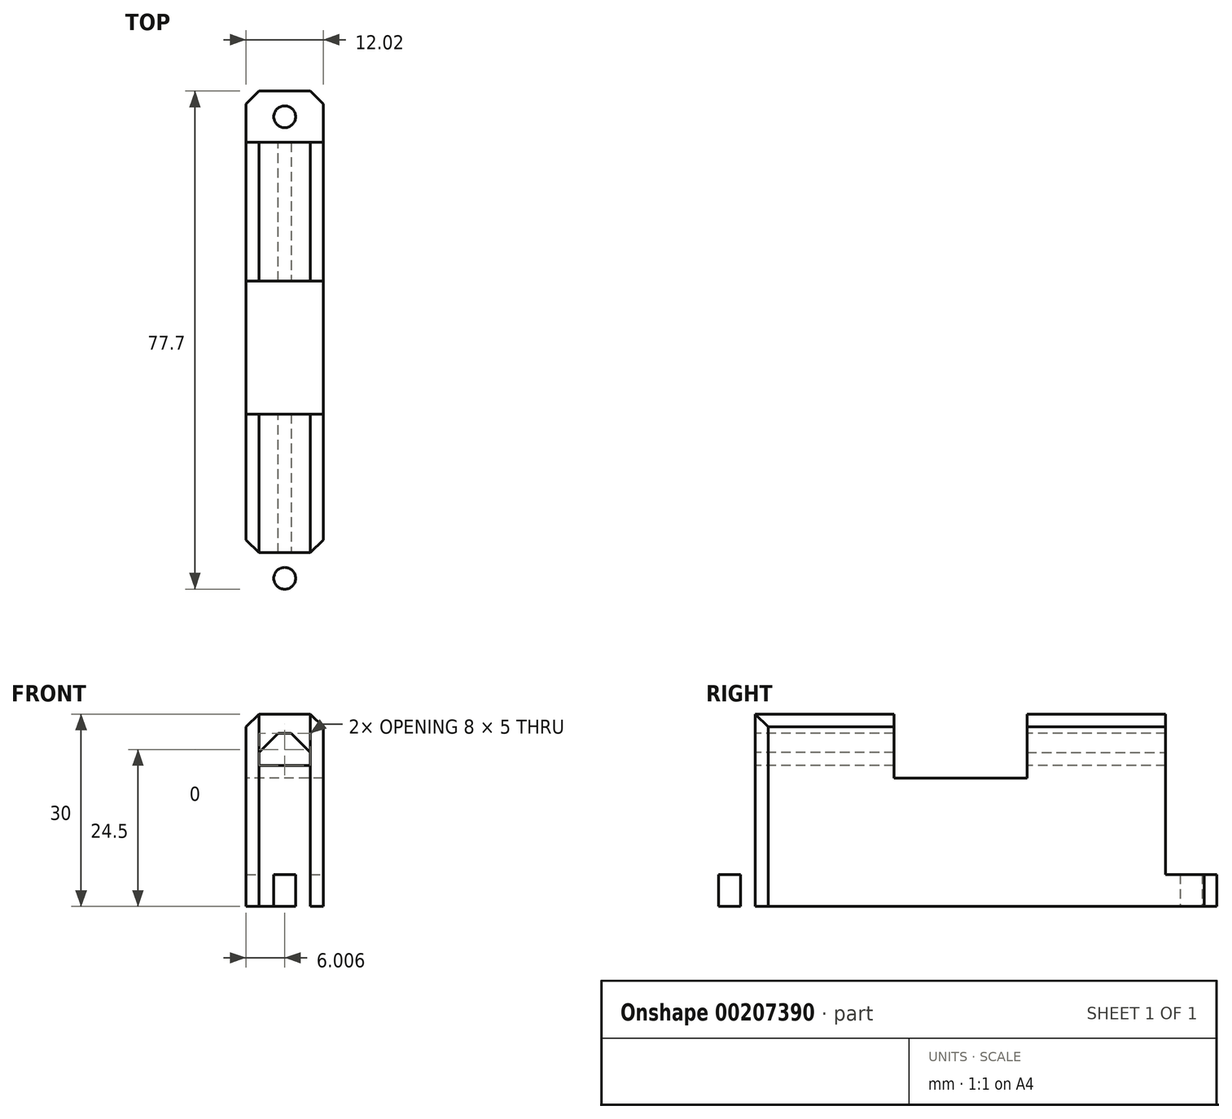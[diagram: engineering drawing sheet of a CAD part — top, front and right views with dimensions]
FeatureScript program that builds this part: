
annotation { "Feature Type Name" : "Feature", "Feature Type Description" : "" }
export const myFeature = defineFeature(function(context is Context, id is Id, definition is map)
    precondition{}
    {
        {
            var Q0;
            Q0=qCreatedBy(makeId("Top.planeOp"),FACE);
            var sketch = newSketch(context, id + "F0", { "sketchPlane" : qUnion([Q0])});
            skLineSegment(sketch, "E0.left", {"start": v(29.65, -22.25) * mm, "end": v(29.65, -43.87) * mm});
            skLineSegment(sketch, "E1", {"start": v(20.9, -54.25) * mm, "end": v(35.66, -54.25) * mm, "construction": true});
            skLineSegment(sketch, "E2", {"start": v(29.65, -43.87) * mm, "end": v(35.66, -43.87) * mm});
            skLineSegment(sketch, "E3", {"start": v(35.66, -54.25) * mm, "end": v(35.66, -22.25) * mm, "construction": true});
            skLineSegment(sketch, "E4.1.MirrorCS", {"start": v(41.67, -22.25) * mm, "end": v(41.67, -43.87) * mm});
            skLineSegment(sketch, "E5.0.MirrorCS", {"start": v(50.4, -54.25) * mm, "end": v(35.66, -54.25) * mm, "construction": true});
            skLineSegment(sketch, "E6.0.MirrorCS", {"start": v(41.67, -43.87) * mm, "end": v(35.66, -43.87) * mm});
            skLineSegment(sketch, "E7", {"start": v(29.65, -43.87) * mm, "end": v(29.65, -54.25) * mm});
            skLineSegment(sketch, "E8.0.MirrorCS", {"start": v(41.67, -43.87) * mm, "end": v(41.67, -54.25) * mm});
            skLineSegment(sketch, "E9", {"start": v(29.65, -22.25) * mm, "end": v(41.67, -22.25) * mm});
            skLineSegment(sketch, "E10", {"start": v(29.65, -22.25) * mm, "end": v(29.65, -14.25) * mm});
            skLineSegment(sketch, "E11", {"start": v(29.65, -14.25) * mm, "end": v(41.67, -14.25) * mm});
            skLineSegment(sketch, "E12", {"start": v(41.67, -14.25) * mm, "end": v(41.67, -22.25) * mm});
            skCircle(sketch, "E13", {"center": v(35.66, -18.25) * mm, "radius": 1.7 * mm});
            skPoint(sketch, "E13.centerSnap0", {"position": v(41.67, -18.25) * mm});
            skCircle(sketch, "E14.MirrorC", {"center": v(35.66, -90.25) * mm, "radius": 1.7 * mm});
            skLineSegment(sketch, "E15.MirrorCS", {"start": v(41.67, -94.25) * mm, "end": v(41.67, -86.25) * mm});
            skPoint(sketch, "E16.MirrorP", {"position": v(41.67, -90.25) * mm});
            skLineSegment(sketch, "E17.MirrorCS", {"start": v(29.65, -94.25) * mm, "end": v(41.67, -94.25) * mm});
            skLineSegment(sketch, "E18.MirrorCS", {"start": v(35.66, -54.25) * mm, "end": v(35.66, -86.25) * mm, "construction": true});
            skLineSegment(sketch, "E19.MirrorCS", {"start": v(29.65, -86.25) * mm, "end": v(29.65, -94.25) * mm});
            skLineSegment(sketch, "E20.MirrorCS", {"start": v(41.67, -86.25) * mm, "end": v(41.67, -64.64) * mm});
            skLineSegment(sketch, "E21.MirrorCS", {"start": v(41.67, -64.64) * mm, "end": v(35.66, -64.64) * mm});
            skLineSegment(sketch, "E22.MirrorCS", {"start": v(29.65, -86.25) * mm, "end": v(29.65, -64.64) * mm});
            skLineSegment(sketch, "E23.MirrorCS", {"start": v(29.65, -64.64) * mm, "end": v(29.65, -54.25) * mm});
            skLineSegment(sketch, "E24.MirrorCS", {"start": v(41.67, -64.64) * mm, "end": v(41.67, -54.25) * mm});
            skLineSegment(sketch, "E25.MirrorCS", {"start": v(29.65, -86.25) * mm, "end": v(41.67, -86.25) * mm});
            skLineSegment(sketch, "E26.MirrorCS", {"start": v(29.65, -64.64) * mm, "end": v(35.66, -64.64) * mm});
            skSolve(sketch);
        }
        {
            var Q0;
            Q0=makeQuery(id+"F0.imprint","IMPRINT",FACE,{"disambiguationData":[TD([[makeQuery(id+"F0.imprint","IMPRINT",EDGE,{"derivedFrom":sQuery(id+"F0.wireOp",EDGE,"E9")}),1.0]])]});
            var Q1;
            Q1=makeQuery(id+"F0.imprint","IMPRINT",FACE,{"disambiguationData":[TD([[makeQuery(id+"F0.imprint","IMPRINT",EDGE,{"derivedFrom":sQuery(id+"F0.wireOp",EDGE,"E0.left")}),1.0]])]});
            var Q2;
            Q2=makeQuery(id+"F0.imprint","IMPRINT",FACE,{"disambiguationData":[TD([[makeQuery(id+"F0.imprint","IMPRINT",EDGE,{"derivedFrom":sQuery(id+"F0.wireOp",EDGE,"E2")}),-1.0]])]});
            var Q3;
            Q3=makeQuery(id+"F0.imprint","IMPRINT",FACE,{"disambiguationData":[TD([[makeQuery(id+"F0.imprint","IMPRINT",EDGE,{"derivedFrom":sQuery(id+"F0.wireOp",EDGE,"E20.MirrorCS")}),1.0]])]});
            var Q4;
            Q4=makeQuery(id+"F0.imprint","IMPRINT",FACE,{"disambiguationData":[TD([[makeQuery(id+"F0.imprint","IMPRINT",EDGE,{"derivedFrom":sQuery(id+"F0.wireOp",EDGE,"E14.MirrorC")}),1.0]])]});
            extrude(context, id + "F1", {"entities" : qUnion([Q0, Q1, Q2, Q3, Q4]), "depth" : 5 * mm});
        }
        {
            var Q0;
            Q0=makeQuery(id+"F0.imprint","IMPRINT",FACE,{"disambiguationData":[TD([[makeQuery(id+"F0.imprint","IMPRINT",EDGE,{"derivedFrom":sQuery(id+"F0.wireOp",EDGE,"E0.left")}),1.0]])]});
            var Q1;
            Q1=makeQuery(id+"F0.imprint","IMPRINT",FACE,{"disambiguationData":[TD([[makeQuery(id+"F0.imprint","IMPRINT",EDGE,{"derivedFrom":sQuery(id+"F0.wireOp",EDGE,"E20.MirrorCS")}),1.0]])]});
            extrude(context, id + "F2", {"entities" : qUnion([Q0, Q1]), "operationType" : NewBodyOperationType.ADD, "depth" : 30 * mm});
        }
        {
            var Q0;
            Q0=makeQuery(id+"F0.imprint","IMPRINT",FACE,{"disambiguationData":[TD([[makeQuery(id+"F0.imprint","IMPRINT",EDGE,{"derivedFrom":sQuery(id+"F0.wireOp",EDGE,"E2")}),-1.0]])]});
            extrude(context, id + "F3", {"entities" : qUnion([Q0]), "operationType" : NewBodyOperationType.ADD, "depth" : 20 * mm});
        }
        {
            var Q0;
            Q0=makeQuery(id+"F2.opExtrude","SWEPT_FACE",FACE,{"disambiguationData":[OSD([sQuery(id+"F0.wireOp",EDGE,"E25.MirrorCS")])]});
            var sketch = newSketch(context, id + "F4", { "sketchPlane" : qUnion([Q0])});
            skLineSegment(sketch, "E27.bottom", {"start": v(31.66, 27) * mm, "end": v(39.66, 27) * mm});
            skLineSegment(sketch, "E27.top", {"start": v(31.66, 22) * mm, "end": v(39.66, 22) * mm});
            skLineSegment(sketch, "E27.left", {"start": v(31.66, 27) * mm, "end": v(31.66, 22) * mm});
            skLineSegment(sketch, "E27.right", {"start": v(39.66, 27) * mm, "end": v(39.66, 22) * mm});
            skPoint(sketch, "E28", {"position": v(35.66, 27) * mm});
            skSolve(sketch);
        }
        {
            var Q0;
            Q0=makeQuery(id+"F4.imprint","IMPRINT",FACE,{"disambiguationData":[TD([[makeQuery(id+"F4.imprint","IMPRINT",EDGE,{"derivedFrom":sQuery(id+"F4.wireOp",EDGE,"E27.bottom")}),-1.0]])]});
            extrude(context, id + "F5", {"entities" : qUnion([Q0]), "operationType" : NewBodyOperationType.REMOVE, "endBound" : BoundingType.THROUGH_ALL, "oppositeDirection" : true, "depth" : 25 * mm});
        }
        {
            var Q0;
            Q0=makeQuery(id+"F5.boolean.opBoolean","COPY",EDGE,{"disambiguationData":[OD(0.0)],"derivedFrom":makeQuery(id+"F5.opExtrude","SWEPT_EDGE",EDGE,{"disambiguationData":[OSD([sQuery(id+"F4.wireOp",EDGE,"E27.bottom"),sQuery(id+"F4.wireOp",EDGE,"E27.left")])]})});
            var Q1;
            Q1=makeQuery(id+"F5.boolean.opBoolean","COPY",EDGE,{"disambiguationData":[OD(0.0)],"derivedFrom":makeQuery(id+"F5.opExtrude","SWEPT_EDGE",EDGE,{"disambiguationData":[OSD([sQuery(id+"F4.wireOp",EDGE,"E27.bottom"),sQuery(id+"F4.wireOp",EDGE,"E27.right")])]})});
            var Q2;
            Q2=makeQuery(id+"F5.boolean.opBoolean","COPY",EDGE,{"disambiguationData":[OD(1.0)],"derivedFrom":makeQuery(id+"F5.opExtrude","SWEPT_EDGE",EDGE,{"disambiguationData":[OSD([sQuery(id+"F4.wireOp",EDGE,"E27.bottom"),sQuery(id+"F4.wireOp",EDGE,"E27.left")])]})});
            var Q3;
            Q3=makeQuery(id+"F5.boolean.opBoolean","COPY",EDGE,{"disambiguationData":[OD(1.0)],"derivedFrom":makeQuery(id+"F5.opExtrude","SWEPT_EDGE",EDGE,{"disambiguationData":[OSD([sQuery(id+"F4.wireOp",EDGE,"E27.bottom"),sQuery(id+"F4.wireOp",EDGE,"E27.right")])]})});
            chamfer(context, id + "F6", {"entities" : qUnion([Q0, Q1, Q2, Q3]), "width" : 3 * mm, "tangentPropagation" : true});
        }
        {
            var Q0;
            Q0=makeQuery(id+"F1.opExtrude","SWEPT_EDGE",EDGE,{"disambiguationData":[OSD([sQuery(id+"F0.wireOp",EDGE,"E17.MirrorCS"),sQuery(id+"F0.wireOp",EDGE,"E19.MirrorCS")])]});
            var Q1;
            Q1=makeQuery(id+"F1.opExtrude","SWEPT_EDGE",EDGE,{"disambiguationData":[OSD([sQuery(id+"F0.wireOp",EDGE,"E15.MirrorCS"),sQuery(id+"F0.wireOp",EDGE,"E17.MirrorCS")])]});
            var Q2;
            Q2=makeQuery(id+"F1.opExtrude","SWEPT_EDGE",EDGE,{"disambiguationData":[OSD([sQuery(id+"F0.wireOp",EDGE,"E10"),sQuery(id+"F0.wireOp",EDGE,"E11")])]});
            var Q3;
            Q3=makeQuery(id+"F1.opExtrude","SWEPT_EDGE",EDGE,{"disambiguationData":[OSD([sQuery(id+"F0.wireOp",EDGE,"E11"),sQuery(id+"F0.wireOp",EDGE,"E12")])]});
            var Q4;
            Q4=makeQuery(id+"F2.opExtrude","CAP_EDGE",EDGE,{"disambiguationData":[OSD([sQuery(id+"F0.wireOp",EDGE,"E4.1.MirrorCS")])],"isStart":false});
            var Q5;
            Q5=makeQuery(id+"F2.opExtrude","CAP_EDGE",EDGE,{"disambiguationData":[OSD([sQuery(id+"F0.wireOp",EDGE,"E0.left")])],"isStart":false});
            var Q6;
            Q6=makeQuery(id+"F2.opExtrude","CAP_EDGE",EDGE,{"disambiguationData":[OSD([sQuery(id+"F0.wireOp",EDGE,"E22.MirrorCS")])],"isStart":false});
            var Q7;
            Q7=makeQuery(id+"F2.opExtrude","CAP_EDGE",EDGE,{"disambiguationData":[OSD([sQuery(id+"F0.wireOp",EDGE,"E20.MirrorCS")])],"isStart":false});
            chamfer(context, id + "F7", {"entities" : qUnion([Q0, Q1, Q2, Q3, Q4, Q5, Q6, Q7]), "width" : 2 * mm, "tangentPropagation" : true});
        }
    });
